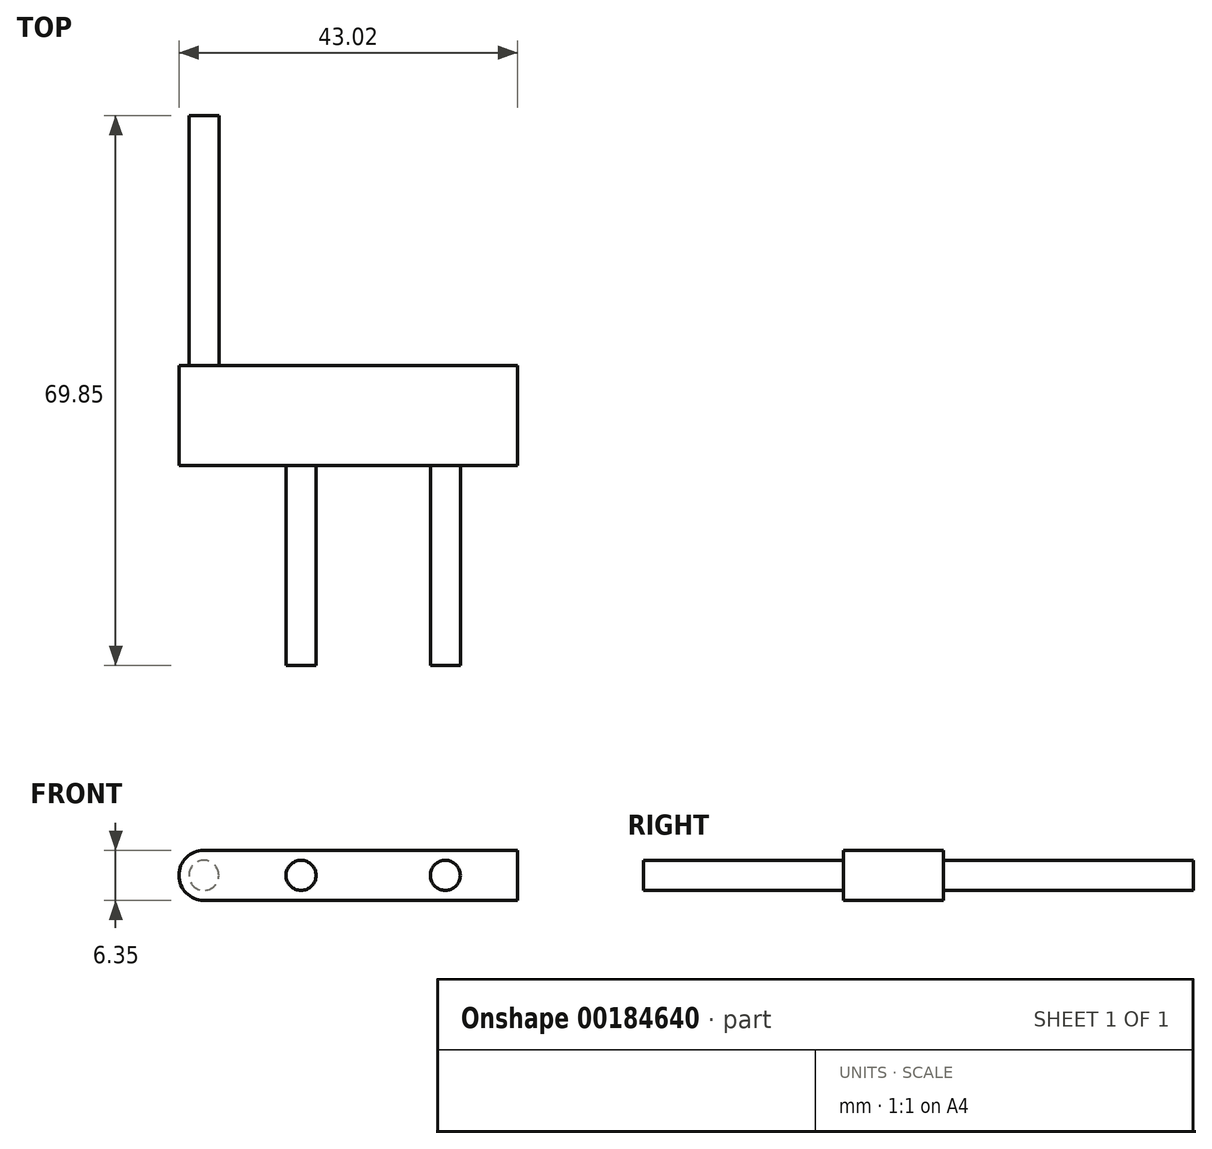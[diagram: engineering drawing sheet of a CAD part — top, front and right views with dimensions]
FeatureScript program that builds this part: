
annotation { "Feature Type Name" : "Feature", "Feature Type Description" : "" }
export const myFeature = defineFeature(function(context is Context, id is Id, definition is map)
    precondition{}
    {
        {
            var Q0;
            Q0=qCreatedBy(makeId("Front.planeOp"),FACE);
            var sketch = newSketch(context, id + "F0", { "sketchPlane" : qUnion([Q0])});
            skLineSegment(sketch, "E0", {"start": v(50.84, -8.86) * mm, "end": v(50.84, -2.5) * mm});
            skLineSegment(sketch, "E1", {"start": v(14.17, -8.86) * mm, "end": v(14.17, -2.5) * mm});
            skLineSegment(sketch, "E2", {"start": v(14.17, -2.5) * mm, "end": v(50.84, -2.5) * mm});
            skPoint(sketch, "E3", {"position": v(14.17, -8.86) * mm});
            skLineSegment(sketch, "E4", {"start": v(50.84, -8.86) * mm, "end": v(14.17, -8.86) * mm});
            skLineSegment(sketch, "E5", {"start": v(14.17, -2.5) * mm, "end": v(11, -2.5) * mm});
            skLineSegment(sketch, "E6", {"start": v(14.17, -8.86) * mm, "end": v(11, -8.86) * mm});
            skPoint(sketch, "E7", {"position": v(11, -5.68) * mm});
            skCircle(sketch, "E8", {"center": v(11, -5.68) * mm, "radius": 3.18 * mm});
            skPoint(sketch, "E9", {"position": v(23.34, -5.68) * mm});
            skPoint(sketch, "E10", {"position": v(41.67, -5.68) * mm});
            skCircle(sketch, "E11", {"center": v(23.34, -5.68) * mm, "radius": 1.9 * mm});
            skCircle(sketch, "E12", {"center": v(41.67, -5.68) * mm, "radius": 1.9 * mm});
            skCircle(sketch, "E13", {"center": v(11, -5.68) * mm, "radius": 1.9 * mm});
            skLineSegment(sketch, "E14", {"start": v(48, -2.5) * mm, "end": v(48, -8.86) * mm});
            skSolve(sketch);
        }
        {
            var Q0;
            Q0 = qSketchRegion(id + "F0", true);
            var Q1;
            Q1=makeQuery(id+"F0.imprint","IMPRINT",FACE,{"disambiguationData":[TD([[makeQuery(id+"F0.imprint","IMPRINT",EDGE,{"derivedFrom":sQuery(id+"F0.wireOp",EDGE,"E11")}),1.0]])]});
            var Q2;
            Q2=makeQuery(id+"F0.imprint","IMPRINT",FACE,{"disambiguationData":[TD([[makeQuery(id+"F0.imprint","IMPRINT",EDGE,{"derivedFrom":sQuery(id+"F0.wireOp",EDGE,"E12")}),1.0]])]});
            var Q3;
            Q3=makeQuery(id+"F0.imprint","IMPRINT",FACE,{"disambiguationData":[TD([[makeQuery(id+"F0.imprint","IMPRINT",EDGE,{"derivedFrom":sQuery(id+"F0.wireOp",EDGE,"E13")}),1.0]])]});
            extrude(context, id + "F1", {"entities" : qUnion([Q0, Q1, Q2, Q3]), "depth" : 12.7 * mm});
        }
        {
            var Q0;
            Q0=makeQuery(id+"F0.imprint","IMPRINT",FACE,{"disambiguationData":[TD([[makeQuery(id+"F0.imprint","IMPRINT",EDGE,{"derivedFrom":sQuery(id+"F0.wireOp",EDGE,"E11")}),1.0]])]});
            var Q1;
            Q1=makeQuery(id+"F0.imprint","IMPRINT",FACE,{"disambiguationData":[TD([[makeQuery(id+"F0.imprint","IMPRINT",EDGE,{"derivedFrom":sQuery(id+"F0.wireOp",EDGE,"E12")}),1.0]])]});
            extrude(context, id + "F2", {"entities" : qUnion([Q0, Q1]), "operationType" : NewBodyOperationType.ADD, "depth" : 38.1 * mm});
        }
        {
            var Q0;
            Q0=makeQuery(id+"F0.imprint","IMPRINT",FACE,{"disambiguationData":[TD([[makeQuery(id+"F0.imprint","IMPRINT",EDGE,{"derivedFrom":sQuery(id+"F0.wireOp",EDGE,"E13")}),1.0]])]});
            extrude(context, id + "F3", {"entities" : qUnion([Q0]), "operationType" : NewBodyOperationType.ADD, "oppositeDirection" : true, "depth" : 31.75 * mm});
        }
    });
